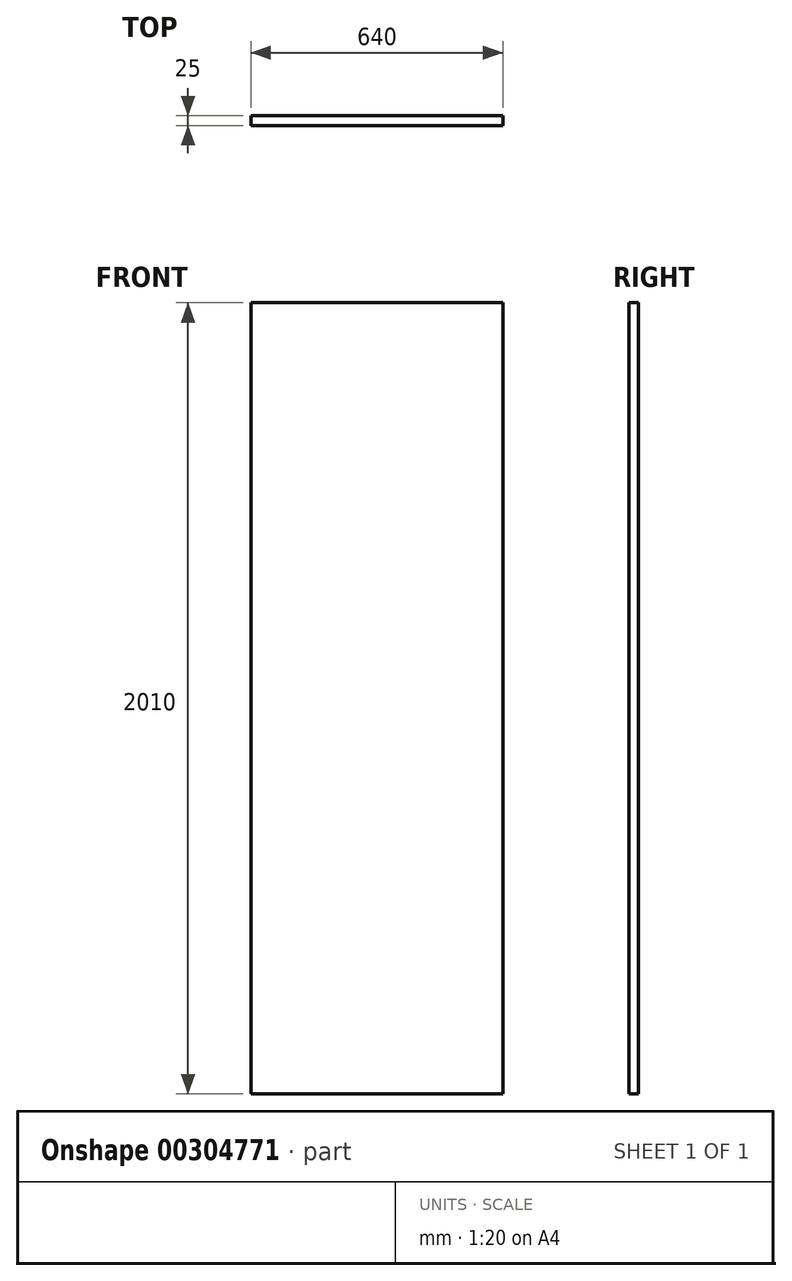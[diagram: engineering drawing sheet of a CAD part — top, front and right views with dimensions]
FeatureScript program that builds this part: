
annotation { "Feature Type Name" : "Feature", "Feature Type Description" : "" }
export const myFeature = defineFeature(function(context is Context, id is Id, definition is map)
    precondition{}
    {
        {
            var Q0;
            Q0=qCreatedBy(makeId("Front.planeOp"),FACE);
            var sketch = newSketch(context, id + "F0", { "sketchPlane" : qUnion([Q0])});
            skLineSegment(sketch, "E0.bottom", {"start": v(320, 1005) * mm, "end": v(-320, 1005) * mm});
            skLineSegment(sketch, "E0.top", {"start": v(320, -1005) * mm, "end": v(-320, -1005) * mm});
            skLineSegment(sketch, "E0.left", {"start": v(320, 1005) * mm, "end": v(320, -1005) * mm});
            skLineSegment(sketch, "E0.right", {"start": v(-320, 1005) * mm, "end": v(-320, -1005) * mm});
            skPoint(sketch, "E0.middle", {"position": v(0, 0) * mm});
            skSolve(sketch);
        }
        {
            var Q0;
            Q0=makeQuery(id+"F0.imprint","IMPRINT",FACE,{"disambiguationData":[TD([[makeQuery(id+"F0.imprint","IMPRINT",EDGE,{"derivedFrom":sQuery(id+"F0.wireOp",EDGE,"E0.bottom")}),1.0]])]});
            extrude(context, id + "F1", {"entities" : qUnion([Q0]), "depth" : 25 * mm});
        }
    });
